# Revit family: 02.Wichmann Kabelbox WD90 rund_WAND
name_source: partatom
category: Mechanical Equipment
revit_build: Autodesk Revit 2018 (Build: 20170223_1515(x64)
units: mm (PartAtom-declared; Revit-internal decimal feet)

## family parameters
Always vertical = Yes
Classification = None
Cut with Voids When Loaded = No
Host = Wall
OmniClass Number = 23.30.20.00
OmniClass Title = Windows
Part Type = Normal
Room Calculation Point = No
Round Connector Dimension = Use Diameter
Shared = No

## types (13) — shared parameters
Bautiefe = 270 mm
Werkstoff = Stahl

## per-type parameters (varying)
| type | Diameter inside | Durchmesser | Durchmesser Rohbau | Durchmesser_1 | HAN |
| Kabelbox WD90 rund, 70x270 mm | 56 mm | 70 mm | 90 mm | 69 mm | 00R70 |
| Kabelbox WD90 rund, 80x270 mm | 64 mm | 80 mm | 100 mm  [stored 0.328084 ft] | 79 mm | 00R80 |
| Kabelbox WD90 rund, 90x270 mm | 72 mm  [stored 0.23622 ft] | 90 mm | 110 mm  [stored 0.360892 ft] | 89 mm | 00R90 |
| Kabelbox WD90 rund, 100x270 mm | 80 mm | 100 mm  [stored 0.328084 ft] | 120 mm | 99 mm | 00R100 |
| Kabelbox WD90 rund, 110x270 mm | 88 mm  [stored 0.288714 ft] | 110 mm  [stored 0.360892 ft] | 130 mm  [stored 0.426509 ft] | 109 mm  [stored 0.357612 ft] | 00R110 |
| Kabelbox WD90 rund, 120x270 mm | 96 mm | 120 mm | 140 mm | 119 mm | 00R120 |
| Kabelbox WD90 rund, 130x270 mm | 104 mm | 130 mm  [stored 0.426509 ft] | 150 mm | 129 mm | 00R130 |
| Kabelbox WD90 rund, 140x270 mm | 112 mm | 140 mm | 160 mm | 139 mm | 00R140 |
| Kabelbox WD90 rund, 150x270 mm | 120 mm | 150 mm | 170 mm | 149 mm | 00R150 |
| Kabelbox WD90 rund, 180x270 mm | 144 mm | 180 mm | 200 mm  [stored 0.656168 ft] | 179 mm | 00R180 |
| Kabelbox WD90 rund, 200x270 mm | 160 mm | 200 mm  [stored 0.656168 ft] | 220 mm | 199 mm | 00R200 |
| Kabelbox WD90 rund, 230x270 mm | 184 mm | 230 mm | 250 mm | 229 mm | 00R230 |
| Kabelbox WD90 rund, 250x270 mm | 200 mm  [stored 0.656168 ft] | 250 mm | 270 mm | 249 mm | 00R250 |

note: [stored X ft] marks values corroborated as IEEE doubles in the binary element streams (Revit-internal decimal feet)

## geometry (parser evidence)
native form markers: Sweep x6
no freeform markers — native parametric forms only
